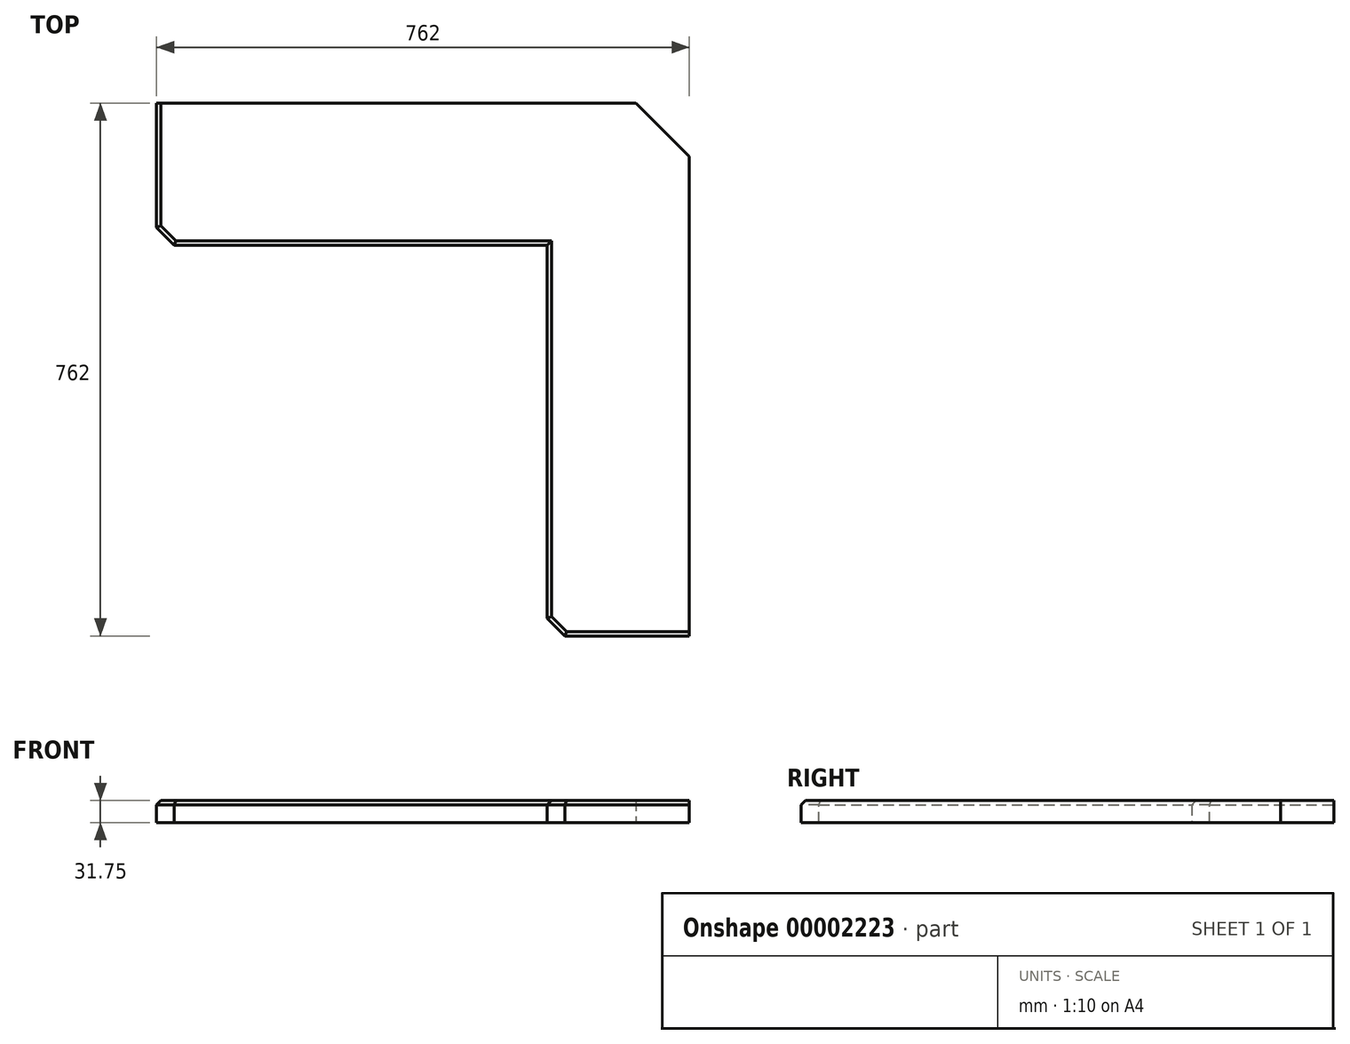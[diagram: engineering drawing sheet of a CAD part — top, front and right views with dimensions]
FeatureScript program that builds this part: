
annotation { "Feature Type Name" : "Feature", "Feature Type Description" : "" }
export const myFeature = defineFeature(function(context is Context, id is Id, definition is map)
    precondition{}
    {
        {
            var Q0;
            Q0=qCreatedBy(makeId("Top.planeOp"),FACE);
            var sketch = newSketch(context, id + "F0", { "sketchPlane" : qUnion([Q0])});
            skLineSegment(sketch, "E0", {"start": v(0, 0) * mm, "end": v(-762, 0) * mm});
            skLineSegment(sketch, "E1", {"start": v(-762, 0) * mm, "end": v(-762, -203.2) * mm});
            skLineSegment(sketch, "E2", {"start": v(-762, -203.2) * mm, "end": v(-203.2, -203.2) * mm});
            skLineSegment(sketch, "E3", {"start": v(-203.2, -203.2) * mm, "end": v(-203.2, -762) * mm});
            skLineSegment(sketch, "E4", {"start": v(-203.2, -762) * mm, "end": v(0, -762) * mm});
            skLineSegment(sketch, "E5", {"start": v(0, -762) * mm, "end": v(0, 0) * mm});
            skSolve(sketch);
        }
        {
            var Q0;
            Q0=makeQuery(id+"F0.imprint","IMPRINT",FACE,{"disambiguationData":[TD([[makeQuery(id+"F0.imprint","IMPRINT",EDGE,{"derivedFrom":sQuery(id+"F0.wireOp",EDGE,"E0")}),1.0]])]});
            extrude(context, id + "F1", {"entities" : qUnion([Q0]), "depth" : 31.75 * mm});
        }
        {
            var Q0;
            Q0=makeQuery(id+"F1.opExtrude","SWEPT_EDGE",EDGE,{"disambiguationData":[OSD([sQuery(id+"F0.wireOp",EDGE,"E1"),sQuery(id+"F0.wireOp",EDGE,"E2")])]});
            var Q1;
            Q1=makeQuery(id+"F1.opExtrude","SWEPT_EDGE",EDGE,{"disambiguationData":[OSD([sQuery(id+"F0.wireOp",EDGE,"E3"),sQuery(id+"F0.wireOp",EDGE,"E4")])]});
            chamfer(context, id + "F2", {"entities" : qUnion([Q0, Q1]), "width" : 25.4 * mm, "tangentPropagation" : true});
        }
        {
            var Q0;
            Q0=makeQuery(id+"F1.opExtrude","CAP_EDGE",EDGE,{"disambiguationData":[OSD([sQuery(id+"F0.wireOp",EDGE,"E1")])],"isStart":false});
            var Q1;
            {var subQ0=sQuery(id+"F0.wireOp",EDGE,"E1");var subQ1=sQuery(id+"F0.wireOp",EDGE,"E2");Q1=makeQuery(id+"F2.opChamfer","BLEND_EDGE",EDGE,{"blendedFrom":[makeQuery(id+"F1.opExtrude","SWEPT_EDGE",EDGE,{"disambiguationData":[OSD([subQ0,subQ1])]}),makeQuery(id+"F1.opExtrude","CAP_FACE",FACE,{"disambiguationData":[OSD([sQuery(id+"F0.wireOp",EDGE,"E0"),subQ0,subQ1,sQuery(id+"F0.wireOp",EDGE,"E3"),sQuery(id+"F0.wireOp",EDGE,"E4"),sQuery(id+"F0.wireOp",EDGE,"E5")])],"isStart":false})],"blendedInto":[makeQuery(id+"F1.opExtrude","CAP_FACE",FACE,{"disambiguationData":[OSD([sQuery(id+"F0.wireOp",EDGE,"E0"),subQ0,subQ1,sQuery(id+"F0.wireOp",EDGE,"E3"),sQuery(id+"F0.wireOp",EDGE,"E4"),sQuery(id+"F0.wireOp",EDGE,"E5")])],"isStart":false})]});}
            var Q2;
            Q2=makeQuery(id+"F1.opExtrude","CAP_EDGE",EDGE,{"disambiguationData":[OSD([sQuery(id+"F0.wireOp",EDGE,"E2")])],"isStart":false});
            var Q3;
            Q3=makeQuery(id+"F1.opExtrude","CAP_EDGE",EDGE,{"disambiguationData":[OSD([sQuery(id+"F0.wireOp",EDGE,"E3")])],"isStart":false});
            var Q4;
            {var subQ0=sQuery(id+"F0.wireOp",EDGE,"E3");var subQ1=sQuery(id+"F0.wireOp",EDGE,"E4");Q4=makeQuery(id+"F2.opChamfer","BLEND_EDGE",EDGE,{"blendedFrom":[makeQuery(id+"F1.opExtrude","SWEPT_EDGE",EDGE,{"disambiguationData":[OSD([subQ0,subQ1])]}),makeQuery(id+"F1.opExtrude","CAP_FACE",FACE,{"disambiguationData":[OSD([sQuery(id+"F0.wireOp",EDGE,"E0"),sQuery(id+"F0.wireOp",EDGE,"E1"),sQuery(id+"F0.wireOp",EDGE,"E2"),subQ0,subQ1,sQuery(id+"F0.wireOp",EDGE,"E5")])],"isStart":false})],"blendedInto":[makeQuery(id+"F1.opExtrude","CAP_FACE",FACE,{"disambiguationData":[OSD([sQuery(id+"F0.wireOp",EDGE,"E0"),sQuery(id+"F0.wireOp",EDGE,"E1"),sQuery(id+"F0.wireOp",EDGE,"E2"),subQ0,subQ1,sQuery(id+"F0.wireOp",EDGE,"E5")])],"isStart":false})]});}
            var Q5;
            Q5=makeQuery(id+"F1.opExtrude","CAP_EDGE",EDGE,{"disambiguationData":[OSD([sQuery(id+"F0.wireOp",EDGE,"E4")])],"isStart":false});
            chamfer(context, id + "F3", {"entities" : qUnion([Q0, Q1, Q2, Q3, Q4, Q5]), "width" : 6.35 * mm, "tangentPropagation" : true});
        }
        {
            var Q0;
            Q0=makeQuery(id+"F1.opExtrude","SWEPT_EDGE",EDGE,{"disambiguationData":[OSD([sQuery(id+"F0.wireOp",EDGE,"E0"),sQuery(id+"F0.wireOp",EDGE,"E5")])]});
            chamfer(context, id + "F4", {"entities" : qUnion([Q0]), "width" : 76.2 * mm, "tangentPropagation" : true});
        }
    });
